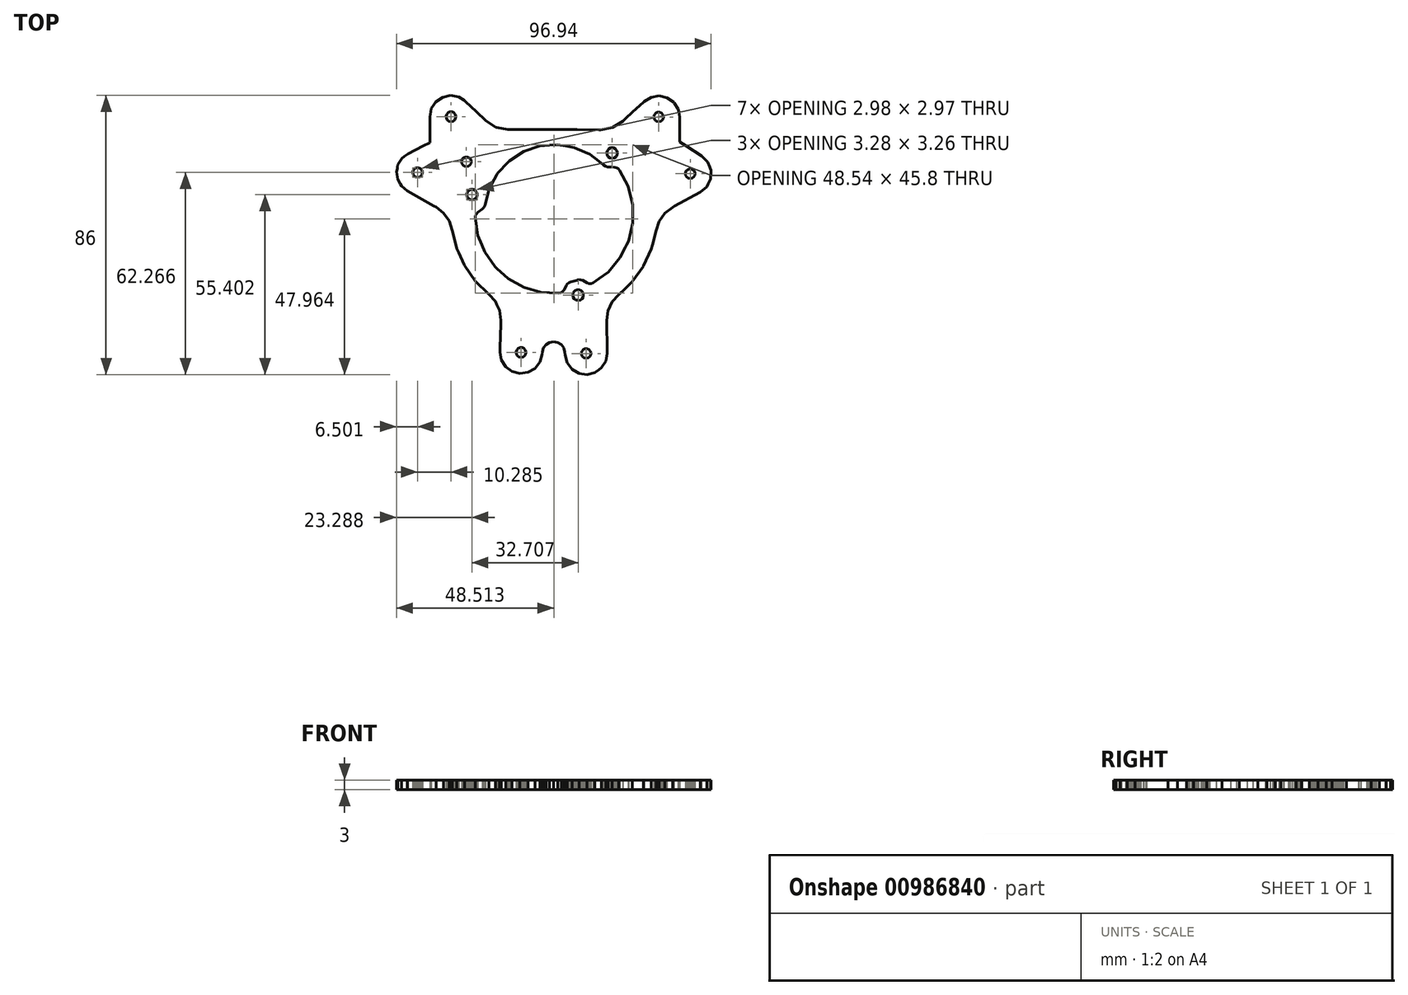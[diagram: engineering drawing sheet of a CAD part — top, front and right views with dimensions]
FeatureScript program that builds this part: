
annotation { "Feature Type Name" : "Feature", "Feature Type Description" : "" }
export const myFeature = defineFeature(function(context is Context, id is Id, definition is map)
    precondition{}
    {
        {
            var Q0;
            Q0=qCreatedBy(makeId("Top.planeOp"),FACE);
            var sketch = newSketch(context, id + "F0", { "sketchPlane" : qUnion([Q0])});
            skLineSegment(sketch, "E0", {"start": v(-20, -18.27) * mm, "end": v(-17.98, -20.51) * mm});
            skLineSegment(sketch, "E1", {"start": v(-17.98, -20.51) * mm, "end": v(-17.54, -21.47) * mm});
            skLineSegment(sketch, "E2", {"start": v(-17.54, -21.47) * mm, "end": v(-16.72, -23.25) * mm});
            skLineSegment(sketch, "E3", {"start": v(-16.72, -23.25) * mm, "end": v(-16.33, -26.24) * mm});
            skLineSegment(sketch, "E4", {"start": v(-20.99, 35.26) * mm, "end": v(-23.77, 37.92) * mm});
            skLineSegment(sketch, "E5", {"start": v(-23.77, 37.92) * mm, "end": v(-27.19, 41.2) * mm});
            skLineSegment(sketch, "E6", {"start": v(-24.23, 5.27) * mm, "end": v(-24.15, 5.93) * mm});
            skLineSegment(sketch, "E7", {"start": v(-24.15, 5.93) * mm, "end": v(-23.85, 6.53) * mm});
            skLineSegment(sketch, "E8", {"start": v(-23.85, 6.53) * mm, "end": v(-23.38, 7) * mm});
            skLineSegment(sketch, "E9", {"start": v(38.82, 28.73) * mm, "end": v(38.82, 31.38) * mm});
            skLineSegment(sketch, "E10", {"start": v(38.82, 31.38) * mm, "end": v(38.82, 36.37) * mm});
            skLineSegment(sketch, "E11", {"start": v(3.87, -15.55) * mm, "end": v(3.21, -16.84) * mm});
            skLineSegment(sketch, "E12", {"start": v(10.22, -14.77) * mm, "end": v(8.92, -14.03) * mm});
            skLineSegment(sketch, "E13", {"start": v(27.92, 41.18) * mm, "end": v(27.64, 40.92) * mm});
            skLineSegment(sketch, "E14", {"start": v(27.64, 40.92) * mm, "end": v(24.37, 37.92) * mm});
            skLineSegment(sketch, "E15", {"start": v(24.37, 37.92) * mm, "end": v(22.05, 35.79) * mm});
            skLineSegment(sketch, "E16", {"start": v(22.05, 35.79) * mm, "end": v(21.26, 35.07) * mm});
            skLineSegment(sketch, "E17", {"start": v(-38.18, 36.5) * mm, "end": v(-38.18, 31.38) * mm});
            skLineSegment(sketch, "E18", {"start": v(-38.18, 31.38) * mm, "end": v(-38.18, 28.5) * mm});
            skLineSegment(sketch, "E19", {"start": v(20.06, -18.4) * mm, "end": v(22.05, -16.48) * mm});
            skLineSegment(sketch, "E20", {"start": v(22.05, -16.48) * mm, "end": v(24.25, -14.35) * mm});
            skLineSegment(sketch, "E21", {"start": v(24.25, -14.35) * mm, "end": v(27.63, -9.6) * mm});
            skLineSegment(sketch, "E22", {"start": v(27.63, -9.6) * mm, "end": v(27.64, -9.56) * mm});
            skLineSegment(sketch, "E23", {"start": v(27.64, -9.56) * mm, "end": v(30.08, -4.3) * mm});
            skLineSegment(sketch, "E24", {"start": v(30.08, -4.3) * mm, "end": v(30.4, -3.06) * mm});
            skLineSegment(sketch, "E25", {"start": v(30.4, -3.06) * mm, "end": v(31.53, 1.35) * mm});
            skLineSegment(sketch, "E26", {"start": v(-44.91, 25.08) * mm, "end": v(-45.97, 24.27) * mm});
            skLineSegment(sketch, "E27", {"start": v(-45.97, 24.27) * mm, "end": v(-46.76, 23.67) * mm});
            skLineSegment(sketch, "E28", {"start": v(-46.76, 23.67) * mm, "end": v(-48, 21.7) * mm});
            skLineSegment(sketch, "E29", {"start": v(-48, 21.7) * mm, "end": v(-48.16, 20.92) * mm});
            skLineSegment(sketch, "E30", {"start": v(-48.16, 20.92) * mm, "end": v(-48.23, 20.58) * mm});
            skLineSegment(sketch, "E31", {"start": v(-48.23, 20.58) * mm, "end": v(-48.47, 19.43) * mm});
            skLineSegment(sketch, "E32", {"start": v(-48.47, 19.43) * mm, "end": v(-48.1, 17.14) * mm});
            skLineSegment(sketch, "E33", {"start": v(-48.1, 17.14) * mm, "end": v(-47.3, 15.72) * mm});
            skLineSegment(sketch, "E34", {"start": v(-47.3, 15.72) * mm, "end": v(-46.96, 15.11) * mm});
            skLineSegment(sketch, "E35", {"start": v(-46.96, 15.11) * mm, "end": v(-45.97, 14.3) * mm});
            skLineSegment(sketch, "E36", {"start": v(-45.97, 14.3) * mm, "end": v(-45.17, 13.63) * mm});
            skLineSegment(sketch, "E37", {"start": v(-24.51, 10.91) * mm, "end": v(-25.18, 10.77) * mm});
            skLineSegment(sketch, "E38", {"start": v(-25.18, 10.77) * mm, "end": v(-25.85, 10.91) * mm});
            skLineSegment(sketch, "E39", {"start": v(-25.85, 10.91) * mm, "end": v(-26.4, 11.32) * mm});
            skLineSegment(sketch, "E40", {"start": v(-26.4, 11.32) * mm, "end": v(-26.75, 11.91) * mm});
            skLineSegment(sketch, "E41", {"start": v(-26.75, 11.91) * mm, "end": v(-26.82, 12.6) * mm});
            skLineSegment(sketch, "E42", {"start": v(-26.82, 12.6) * mm, "end": v(-26.61, 13.25) * mm});
            skLineSegment(sketch, "E43", {"start": v(-26.61, 13.25) * mm, "end": v(-26.15, 13.76) * mm});
            skLineSegment(sketch, "E44", {"start": v(-26.15, 13.76) * mm, "end": v(-25.53, 14.03) * mm});
            skLineSegment(sketch, "E45", {"start": v(-25.53, 14.03) * mm, "end": v(-24.84, 14.03) * mm});
            skLineSegment(sketch, "E46", {"start": v(-24.84, 14.03) * mm, "end": v(-24.21, 13.76) * mm});
            skLineSegment(sketch, "E47", {"start": v(-24.21, 13.76) * mm, "end": v(-23.75, 13.25) * mm});
            skLineSegment(sketch, "E48", {"start": v(-23.75, 13.25) * mm, "end": v(-23.54, 12.6) * mm});
            skLineSegment(sketch, "E49", {"start": v(-23.54, 12.6) * mm, "end": v(-23.61, 11.91) * mm});
            skLineSegment(sketch, "E50", {"start": v(-23.61, 11.91) * mm, "end": v(-23.96, 11.32) * mm});
            skLineSegment(sketch, "E51", {"start": v(-23.96, 11.32) * mm, "end": v(-24.51, 10.91) * mm});
            skLineSegment(sketch, "E52", {"start": v(20.33, 19.96) * mm, "end": v(22.05, 16.62) * mm});
            skLineSegment(sketch, "E53", {"start": v(22.05, 16.62) * mm, "end": v(22.5, 15.72) * mm});
            skLineSegment(sketch, "E54", {"start": v(22.5, 15.72) * mm, "end": v(22.93, 14.89) * mm});
            skLineSegment(sketch, "E55", {"start": v(22.93, 14.89) * mm, "end": v(24.29, 9.35) * mm});
            skLineSegment(sketch, "E56", {"start": v(24.29, 9.35) * mm, "end": v(24.31, 3.64) * mm});
            skLineSegment(sketch, "E57", {"start": v(24.31, 3.64) * mm, "end": v(23.01, -1.91) * mm});
            skLineSegment(sketch, "E58", {"start": v(23.01, -1.91) * mm, "end": v(22.44, -3.06) * mm});
            skLineSegment(sketch, "E59", {"start": v(22.44, -3.06) * mm, "end": v(22.05, -3.83) * mm});
            skLineSegment(sketch, "E60", {"start": v(22.05, -3.83) * mm, "end": v(20.46, -7) * mm});
            skLineSegment(sketch, "E61", {"start": v(20.46, -7) * mm, "end": v(16.78, -11.37) * mm});
            skLineSegment(sketch, "E62", {"start": v(16.78, -11.37) * mm, "end": v(13.9, -13.5) * mm});
            skLineSegment(sketch, "E63", {"start": v(13.9, -13.5) * mm, "end": v(12.2, -14.77) * mm});
            skLineSegment(sketch, "E64", {"start": v(16.58, 21) * mm, "end": v(17.73, 20.92) * mm});
            skLineSegment(sketch, "E65", {"start": v(17.73, 20.92) * mm, "end": v(18.81, 20.84) * mm});
            skLineSegment(sketch, "E66", {"start": v(-22.03, 7.95) * mm, "end": v(-21.47, 8.54) * mm});
            skLineSegment(sketch, "E67", {"start": v(-21.47, 8.54) * mm, "end": v(-21.2, 9.31) * mm});
            skLineSegment(sketch, "E68", {"start": v(8.92, -14.03) * mm, "end": v(8.4, -13.83) * mm});
            skLineSegment(sketch, "E69", {"start": v(8.4, -13.83) * mm, "end": v(7.83, -13.78) * mm});
            skLineSegment(sketch, "E70", {"start": v(7.83, -13.78) * mm, "end": v(7.27, -13.89) * mm});
            skLineSegment(sketch, "E71", {"start": v(12.2, -14.77) * mm, "end": v(11.55, -15) * mm});
            skLineSegment(sketch, "E72", {"start": v(11.55, -15) * mm, "end": v(10.86, -15) * mm});
            skLineSegment(sketch, "E73", {"start": v(10.86, -15) * mm, "end": v(10.22, -14.77) * mm});
            skLineSegment(sketch, "E74", {"start": v(3.5, -37.01) * mm, "end": v(4.16, -39.4) * mm});
            skLineSegment(sketch, "E75", {"start": v(4.16, -39.4) * mm, "end": v(5.67, -41.38) * mm});
            skLineSegment(sketch, "E76", {"start": v(5.67, -41.38) * mm, "end": v(7.18, -42.26) * mm});
            skLineSegment(sketch, "E77", {"start": v(7.18, -42.26) * mm, "end": v(7.82, -42.64) * mm});
            skLineSegment(sketch, "E78", {"start": v(7.82, -42.64) * mm, "end": v(10.28, -43) * mm});
            skLineSegment(sketch, "E79", {"start": v(10.28, -43) * mm, "end": v(12.7, -42.41) * mm});
            skLineSegment(sketch, "E80", {"start": v(12.7, -42.41) * mm, "end": v(13.9, -41.54) * mm});
            skLineSegment(sketch, "E81", {"start": v(13.9, -41.54) * mm, "end": v(14.7, -40.96) * mm});
            skLineSegment(sketch, "E82", {"start": v(14.7, -40.96) * mm, "end": v(16.04, -38.86) * mm});
            skLineSegment(sketch, "E83", {"start": v(16.04, -38.86) * mm, "end": v(16.48, -36.41) * mm});
            skLineSegment(sketch, "E84", {"start": v(-31.33, 1.44) * mm, "end": v(-30.2, -3.06) * mm});
            skLineSegment(sketch, "E85", {"start": v(-30.2, -3.06) * mm, "end": v(-29.9, -4.19) * mm});
            skLineSegment(sketch, "E86", {"start": v(-29.9, -4.19) * mm, "end": v(-29.3, -5.5) * mm});
            skLineSegment(sketch, "E87", {"start": v(-29.3, -5.5) * mm, "end": v(-27.63, -9.16) * mm});
            skLineSegment(sketch, "E88", {"start": v(-27.63, -9.16) * mm, "end": v(-27.49, -9.46) * mm});
            skLineSegment(sketch, "E89", {"start": v(-27.49, -9.46) * mm, "end": v(-24.15, -14.2) * mm});
            skLineSegment(sketch, "E90", {"start": v(-24.15, -14.2) * mm, "end": v(-20, -18.27) * mm});
            skLineSegment(sketch, "E91", {"start": v(7.52, -20.19) * mm, "end": v(7.18, -20.11) * mm});
            skLineSegment(sketch, "E92", {"start": v(7.18, -20.11) * mm, "end": v(6.85, -20.04) * mm});
            skLineSegment(sketch, "E93", {"start": v(6.85, -20.04) * mm, "end": v(6.3, -19.64) * mm});
            skLineSegment(sketch, "E94", {"start": v(6.3, -19.64) * mm, "end": v(5.96, -19.05) * mm});
            skLineSegment(sketch, "E95", {"start": v(5.96, -19.05) * mm, "end": v(5.88, -18.36) * mm});
            skLineSegment(sketch, "E96", {"start": v(5.88, -18.36) * mm, "end": v(6.1, -17.71) * mm});
            skLineSegment(sketch, "E97", {"start": v(6.1, -17.71) * mm, "end": v(6.56, -17.2) * mm});
            skLineSegment(sketch, "E98", {"start": v(6.56, -17.2) * mm, "end": v(7.18, -16.92) * mm});
            skLineSegment(sketch, "E99", {"start": v(7.18, -16.92) * mm, "end": v(7.18, -16.92) * mm});
            skLineSegment(sketch, "E100", {"start": v(7.18, -16.92) * mm, "end": v(7.87, -16.92) * mm});
            skLineSegment(sketch, "E101", {"start": v(7.87, -16.92) * mm, "end": v(8.5, -17.2) * mm});
            skLineSegment(sketch, "E102", {"start": v(8.5, -17.2) * mm, "end": v(8.95, -17.71) * mm});
            skLineSegment(sketch, "E103", {"start": v(8.95, -17.71) * mm, "end": v(9.17, -18.36) * mm});
            skLineSegment(sketch, "E104", {"start": v(9.17, -18.36) * mm, "end": v(9.1, -19.05) * mm});
            skLineSegment(sketch, "E105", {"start": v(9.1, -19.05) * mm, "end": v(8.75, -19.64) * mm});
            skLineSegment(sketch, "E106", {"start": v(8.75, -19.64) * mm, "end": v(8.2, -20.04) * mm});
            skLineSegment(sketch, "E107", {"start": v(8.2, -20.04) * mm, "end": v(7.52, -20.19) * mm});
            skLineSegment(sketch, "E108", {"start": v(31.7, 35) * mm, "end": v(31.2, 35.37) * mm});
            skLineSegment(sketch, "E109", {"start": v(31.2, 35.37) * mm, "end": v(30.89, 35.91) * mm});
            skLineSegment(sketch, "E110", {"start": v(30.89, 35.91) * mm, "end": v(30.82, 36.53) * mm});
            skLineSegment(sketch, "E111", {"start": v(30.82, 36.53) * mm, "end": v(31.02, 37.12) * mm});
            skLineSegment(sketch, "E112", {"start": v(31.02, 37.12) * mm, "end": v(31.43, 37.59) * mm});
            skLineSegment(sketch, "E113", {"start": v(31.43, 37.59) * mm, "end": v(32, 37.84) * mm});
            skLineSegment(sketch, "E114", {"start": v(32, 37.84) * mm, "end": v(32.63, 37.84) * mm});
            skLineSegment(sketch, "E115", {"start": v(32.63, 37.84) * mm, "end": v(33.2, 37.59) * mm});
            skLineSegment(sketch, "E116", {"start": v(33.2, 37.59) * mm, "end": v(33.62, 37.12) * mm});
            skLineSegment(sketch, "E117", {"start": v(33.62, 37.12) * mm, "end": v(33.8, 36.53) * mm});
            skLineSegment(sketch, "E118", {"start": v(33.8, 36.53) * mm, "end": v(33.74, 35.91) * mm});
            skLineSegment(sketch, "E119", {"start": v(33.74, 35.91) * mm, "end": v(33.43, 35.37) * mm});
            skLineSegment(sketch, "E120", {"start": v(33.43, 35.37) * mm, "end": v(32.93, 35) * mm});
            skLineSegment(sketch, "E121", {"start": v(32.93, 35) * mm, "end": v(32.32, 34.87) * mm});
            skLineSegment(sketch, "E122", {"start": v(32.32, 34.87) * mm, "end": v(31.7, 35) * mm});
            skLineSegment(sketch, "E123", {"start": v(9.37, -37.88) * mm, "end": v(8.86, -37.5) * mm});
            skLineSegment(sketch, "E124", {"start": v(8.86, -37.5) * mm, "end": v(8.55, -36.97) * mm});
            skLineSegment(sketch, "E125", {"start": v(8.55, -36.97) * mm, "end": v(8.48, -36.35) * mm});
            skLineSegment(sketch, "E126", {"start": v(8.48, -36.35) * mm, "end": v(8.68, -35.75) * mm});
            skLineSegment(sketch, "E127", {"start": v(8.68, -35.75) * mm, "end": v(9.1, -35.3) * mm});
            skLineSegment(sketch, "E128", {"start": v(9.1, -35.3) * mm, "end": v(9.66, -35.04) * mm});
            skLineSegment(sketch, "E129", {"start": v(9.66, -35.04) * mm, "end": v(10.29, -35.04) * mm});
            skLineSegment(sketch, "E130", {"start": v(10.29, -35.04) * mm, "end": v(10.86, -35.3) * mm});
            skLineSegment(sketch, "E131", {"start": v(10.86, -35.3) * mm, "end": v(11.28, -35.75) * mm});
            skLineSegment(sketch, "E132", {"start": v(11.28, -35.75) * mm, "end": v(11.47, -36.35) * mm});
            skLineSegment(sketch, "E133", {"start": v(11.47, -36.35) * mm, "end": v(11.4, -36.97) * mm});
            skLineSegment(sketch, "E134", {"start": v(11.4, -36.97) * mm, "end": v(11.1, -37.5) * mm});
            skLineSegment(sketch, "E135", {"start": v(11.1, -37.5) * mm, "end": v(10.59, -37.88) * mm});
            skLineSegment(sketch, "E136", {"start": v(10.59, -37.88) * mm, "end": v(9.98, -38) * mm});
            skLineSegment(sketch, "E137", {"start": v(9.98, -38) * mm, "end": v(9.37, -37.88) * mm});
            skLineSegment(sketch, "E138", {"start": v(18.81, 20.84) * mm, "end": v(19.4, 20.71) * mm});
            skLineSegment(sketch, "E139", {"start": v(19.4, 20.71) * mm, "end": v(19.63, 20.58) * mm});
            skLineSegment(sketch, "E140", {"start": v(19.63, 20.58) * mm, "end": v(19.92, 20.4) * mm});
            skLineSegment(sketch, "E141", {"start": v(19.92, 20.4) * mm, "end": v(20.33, 19.96) * mm});
            skLineSegment(sketch, "E142", {"start": v(-16.33, -26.24) * mm, "end": v(-16.36, -27.44) * mm});
            skLineSegment(sketch, "E143", {"start": v(-16.36, -27.44) * mm, "end": v(-16.52, -34.85) * mm});
            skLineSegment(sketch, "E144", {"start": v(-16.52, -34.85) * mm, "end": v(-16.55, -36.05) * mm});
            skLineSegment(sketch, "E145", {"start": v(17.3, 23.76) * mm, "end": v(16.75, 24.16) * mm});
            skLineSegment(sketch, "E146", {"start": v(16.75, 24.16) * mm, "end": v(16.41, 24.76) * mm});
            skLineSegment(sketch, "E147", {"start": v(16.41, 24.76) * mm, "end": v(16.34, 25.44) * mm});
            skLineSegment(sketch, "E148", {"start": v(16.34, 25.44) * mm, "end": v(16.55, 26.1) * mm});
            skLineSegment(sketch, "E149", {"start": v(16.55, 26.1) * mm, "end": v(17.01, 26.6) * mm});
            skLineSegment(sketch, "E150", {"start": v(17.01, 26.6) * mm, "end": v(17.64, 26.88) * mm});
            skLineSegment(sketch, "E151", {"start": v(17.64, 26.88) * mm, "end": v(18.32, 26.88) * mm});
            skLineSegment(sketch, "E152", {"start": v(18.32, 26.88) * mm, "end": v(18.95, 26.6) * mm});
            skLineSegment(sketch, "E153", {"start": v(18.95, 26.6) * mm, "end": v(19.4, 26.1) * mm});
            skLineSegment(sketch, "E154", {"start": v(19.4, 26.1) * mm, "end": v(19.62, 25.44) * mm});
            skLineSegment(sketch, "E155", {"start": v(19.62, 25.44) * mm, "end": v(19.55, 24.76) * mm});
            skLineSegment(sketch, "E156", {"start": v(19.55, 24.76) * mm, "end": v(19.2, 24.16) * mm});
            skLineSegment(sketch, "E157", {"start": v(19.2, 24.16) * mm, "end": v(18.65, 23.76) * mm});
            skLineSegment(sketch, "E158", {"start": v(18.65, 23.76) * mm, "end": v(17.98, 23.62) * mm});
            skLineSegment(sketch, "E159", {"start": v(17.98, 23.62) * mm, "end": v(17.3, 23.76) * mm});
            skLineSegment(sketch, "E160", {"start": v(-21.2, 9.31) * mm, "end": v(-19.83, 14.42) * mm});
            skLineSegment(sketch, "E161", {"start": v(-19.83, 14.42) * mm, "end": v(-19.11, 15.72) * mm});
            skLineSegment(sketch, "E162", {"start": v(-19.11, 15.72) * mm, "end": v(-17.54, 18.55) * mm});
            skLineSegment(sketch, "E163", {"start": v(-17.54, 18.55) * mm, "end": v(-17.27, 19.05) * mm});
            skLineSegment(sketch, "E164", {"start": v(-17.27, 19.05) * mm, "end": v(-15.83, 20.58) * mm});
            skLineSegment(sketch, "E165", {"start": v(-15.83, 20.58) * mm, "end": v(-15.5, 20.92) * mm});
            skLineSegment(sketch, "E166", {"start": v(-15.5, 20.92) * mm, "end": v(-13.65, 22.9) * mm});
            skLineSegment(sketch, "E167", {"start": v(-13.65, 22.9) * mm, "end": v(-9.2, 25.77) * mm});
            skLineSegment(sketch, "E168", {"start": v(-9.2, 25.77) * mm, "end": v(-4.34, 27.4) * mm});
            skLineSegment(sketch, "E169", {"start": v(-4.34, 27.4) * mm, "end": v(-4.19, 27.45) * mm});
            skLineSegment(sketch, "E170", {"start": v(-4.19, 27.45) * mm, "end": v(-1.34, 27.67) * mm});
            skLineSegment(sketch, "E171", {"start": v(-1.34, 27.67) * mm, "end": v(1.09, 27.86) * mm});
            skLineSegment(sketch, "E172", {"start": v(1.09, 27.86) * mm, "end": v(3.8, 27.4) * mm});
            skLineSegment(sketch, "E173", {"start": v(3.8, 27.4) * mm, "end": v(6.3, 26.97) * mm});
            skLineSegment(sketch, "E174", {"start": v(6.3, 26.97) * mm, "end": v(7.18, 26.59) * mm});
            skLineSegment(sketch, "E175", {"start": v(7.18, 26.59) * mm, "end": v(11.14, 24.84) * mm});
            skLineSegment(sketch, "E176", {"start": v(11.14, 24.84) * mm, "end": v(13.9, 22.68) * mm});
            skLineSegment(sketch, "E177", {"start": v(13.9, 22.68) * mm, "end": v(15.31, 21.58) * mm});
            skLineSegment(sketch, "E178", {"start": v(45.6, 24.32) * mm, "end": v(40.87, 27.4) * mm});
            skLineSegment(sketch, "E179", {"start": v(40.87, 27.4) * mm, "end": v(38.82, 28.73) * mm});
            skLineSegment(sketch, "E180", {"start": v(-16.55, -36.05) * mm, "end": v(-16.13, -38.5) * mm});
            skLineSegment(sketch, "E181", {"start": v(-16.13, -38.5) * mm, "end": v(-14.82, -40.6) * mm});
            skLineSegment(sketch, "E182", {"start": v(-14.82, -40.6) * mm, "end": v(-12.82, -42.07) * mm});
            skLineSegment(sketch, "E183", {"start": v(-12.82, -42.07) * mm, "end": v(-10.42, -42.68) * mm});
            skLineSegment(sketch, "E184", {"start": v(-10.42, -42.68) * mm, "end": v(-7.96, -42.35) * mm});
            skLineSegment(sketch, "E185", {"start": v(-7.96, -42.35) * mm, "end": v(-5.8, -41.11) * mm});
            skLineSegment(sketch, "E186", {"start": v(-5.8, -41.11) * mm, "end": v(-4.27, -39.17) * mm});
            skLineSegment(sketch, "E187", {"start": v(-4.27, -39.17) * mm, "end": v(-3.58, -36.78) * mm});
            skLineSegment(sketch, "E188", {"start": v(15.31, 21.58) * mm, "end": v(15.9, 21.18) * mm});
            skLineSegment(sketch, "E189", {"start": v(15.9, 21.18) * mm, "end": v(16.58, 21) * mm});
            skLineSegment(sketch, "E190", {"start": v(5.18, -14.5) * mm, "end": v(4.65, -14.72) * mm});
            skLineSegment(sketch, "E191", {"start": v(4.65, -14.72) * mm, "end": v(4.2, -15.08) * mm});
            skLineSegment(sketch, "E192", {"start": v(4.2, -15.08) * mm, "end": v(3.87, -15.55) * mm});
            skLineSegment(sketch, "E193", {"start": v(16.48, -36.41) * mm, "end": v(16.45, -34.85) * mm});
            skLineSegment(sketch, "E194", {"start": v(16.45, -34.85) * mm, "end": v(16.35, -27.44) * mm});
            skLineSegment(sketch, "E195", {"start": v(16.35, -27.44) * mm, "end": v(16.33, -26.34) * mm});
            skLineSegment(sketch, "E196", {"start": v(7.27, -13.89) * mm, "end": v(7.18, -13.92) * mm});
            skLineSegment(sketch, "E197", {"start": v(7.18, -13.92) * mm, "end": v(5.18, -14.5) * mm});
            skLineSegment(sketch, "E198", {"start": v(-3.51, -36.07) * mm, "end": v(-3.16, -34.85) * mm});
            skLineSegment(sketch, "E199", {"start": v(-3.16, -34.85) * mm, "end": v(-3.16, -34.83) * mm});
            skLineSegment(sketch, "E200", {"start": v(-3.16, -34.83) * mm, "end": v(-2.38, -33.8) * mm});
            skLineSegment(sketch, "E201", {"start": v(-2.38, -33.8) * mm, "end": v(-1.34, -33.17) * mm});
            skLineSegment(sketch, "E202", {"start": v(-1.34, -33.17) * mm, "end": v(-1.29, -33.14) * mm});
            skLineSegment(sketch, "E203", {"start": v(-1.29, -33.14) * mm, "end": v(-0.02, -32.9) * mm});
            skLineSegment(sketch, "E204", {"start": v(-0.02, -32.9) * mm, "end": v(1.24, -33.15) * mm});
            skLineSegment(sketch, "E205", {"start": v(1.24, -33.15) * mm, "end": v(2.33, -33.84) * mm});
            skLineSegment(sketch, "E206", {"start": v(2.33, -33.84) * mm, "end": v(3.07, -34.85) * mm});
            skLineSegment(sketch, "E207", {"start": v(3.07, -34.85) * mm, "end": v(3.1, -34.88) * mm});
            skLineSegment(sketch, "E208", {"start": v(3.1, -34.88) * mm, "end": v(3.43, -36.12) * mm});
            skLineSegment(sketch, "E209", {"start": v(-36.28, 8.59) * mm, "end": v(-33.93, 6.74) * mm});
            skLineSegment(sketch, "E210", {"start": v(-33.93, 6.74) * mm, "end": v(-32.23, 4.29) * mm});
            skLineSegment(sketch, "E211", {"start": v(-32.23, 4.29) * mm, "end": v(-31.33, 1.44) * mm});
            skLineSegment(sketch, "E212", {"start": v(-45.17, 13.63) * mm, "end": v(-36.83, 8.9) * mm});
            skLineSegment(sketch, "E213", {"start": v(-36.83, 8.9) * mm, "end": v(-36.28, 8.59) * mm});
            skLineSegment(sketch, "E214", {"start": v(3.21, -16.84) * mm, "end": v(2.8, -17.4) * mm});
            skLineSegment(sketch, "E215", {"start": v(2.8, -17.4) * mm, "end": v(2.22, -17.77) * mm});
            skLineSegment(sketch, "E216", {"start": v(2.22, -17.77) * mm, "end": v(1.55, -17.93) * mm});
            skLineSegment(sketch, "E217", {"start": v(45.15, 13.15) * mm, "end": v(47.19, 14.88) * mm});
            skLineSegment(sketch, "E218", {"start": v(47.19, 14.88) * mm, "end": v(47.6, 15.72) * mm});
            skLineSegment(sketch, "E219", {"start": v(47.6, 15.72) * mm, "end": v(48.36, 17.28) * mm});
            skLineSegment(sketch, "E220", {"start": v(48.36, 17.28) * mm, "end": v(48.47, 19.95) * mm});
            skLineSegment(sketch, "E221", {"start": v(48.47, 19.95) * mm, "end": v(48.22, 20.58) * mm});
            skLineSegment(sketch, "E222", {"start": v(48.22, 20.58) * mm, "end": v(48.09, 20.92) * mm});
            skLineSegment(sketch, "E223", {"start": v(48.09, 20.92) * mm, "end": v(47.5, 22.44) * mm});
            skLineSegment(sketch, "E224", {"start": v(47.5, 22.44) * mm, "end": v(45.6, 24.32) * mm});
            skLineSegment(sketch, "E225", {"start": v(-10.36, -34.72) * mm, "end": v(-9.74, -34.72) * mm});
            skLineSegment(sketch, "E226", {"start": v(-9.74, -34.72) * mm, "end": v(-9.46, -34.85) * mm});
            skLineSegment(sketch, "E227", {"start": v(-9.46, -34.85) * mm, "end": v(-9.17, -34.98) * mm});
            skLineSegment(sketch, "E228", {"start": v(-9.17, -34.98) * mm, "end": v(-8.75, -35.44) * mm});
            skLineSegment(sketch, "E229", {"start": v(-8.75, -35.44) * mm, "end": v(-8.56, -36.03) * mm});
            skLineSegment(sketch, "E230", {"start": v(-8.56, -36.03) * mm, "end": v(-8.62, -36.65) * mm});
            skLineSegment(sketch, "E231", {"start": v(-8.62, -36.65) * mm, "end": v(-8.94, -37.2) * mm});
            skLineSegment(sketch, "E232", {"start": v(-8.94, -37.2) * mm, "end": v(-9.44, -37.56) * mm});
            skLineSegment(sketch, "E233", {"start": v(-9.44, -37.56) * mm, "end": v(-10.05, -37.7) * mm});
            skLineSegment(sketch, "E234", {"start": v(-10.05, -37.7) * mm, "end": v(-10.66, -37.56) * mm});
            skLineSegment(sketch, "E235", {"start": v(-10.66, -37.56) * mm, "end": v(-11.16, -37.2) * mm});
            skLineSegment(sketch, "E236", {"start": v(-11.16, -37.2) * mm, "end": v(-11.48, -36.65) * mm});
            skLineSegment(sketch, "E237", {"start": v(-11.48, -36.65) * mm, "end": v(-11.54, -36.03) * mm});
            skLineSegment(sketch, "E238", {"start": v(-11.54, -36.03) * mm, "end": v(-11.35, -35.44) * mm});
            skLineSegment(sketch, "E239", {"start": v(-11.35, -35.44) * mm, "end": v(-10.93, -34.98) * mm});
            skLineSegment(sketch, "E240", {"start": v(-10.93, -34.98) * mm, "end": v(-10.64, -34.85) * mm});
            skLineSegment(sketch, "E241", {"start": v(-10.64, -34.85) * mm, "end": v(-10.36, -34.72) * mm});
            skLineSegment(sketch, "E242", {"start": v(-23.38, 7) * mm, "end": v(-22.03, 7.95) * mm});
            skLineSegment(sketch, "E243", {"start": v(-14.09, 32.48) * mm, "end": v(-17.54, 33.15) * mm});
            skLineSegment(sketch, "E244", {"start": v(-17.54, 33.15) * mm, "end": v(-17.8, 33.2) * mm});
            skLineSegment(sketch, "E245", {"start": v(-17.8, 33.2) * mm, "end": v(-20.99, 35.26) * mm});
            skLineSegment(sketch, "E246", {"start": v(36.65, 8.57) * mm, "end": v(37.19, 8.86) * mm});
            skLineSegment(sketch, "E247", {"start": v(37.19, 8.86) * mm, "end": v(45.15, 13.15) * mm});
            skLineSegment(sketch, "E248", {"start": v(41.45, 17.5) * mm, "end": v(40.94, 17.87) * mm});
            skLineSegment(sketch, "E249", {"start": v(40.94, 17.87) * mm, "end": v(40.63, 18.41) * mm});
            skLineSegment(sketch, "E250", {"start": v(40.63, 18.41) * mm, "end": v(40.57, 19.03) * mm});
            skLineSegment(sketch, "E251", {"start": v(40.57, 19.03) * mm, "end": v(40.76, 19.62) * mm});
            skLineSegment(sketch, "E252", {"start": v(40.76, 19.62) * mm, "end": v(41.18, 20.09) * mm});
            skLineSegment(sketch, "E253", {"start": v(41.18, 20.09) * mm, "end": v(41.75, 20.34) * mm});
            skLineSegment(sketch, "E254", {"start": v(41.75, 20.34) * mm, "end": v(42.37, 20.34) * mm});
            skLineSegment(sketch, "E255", {"start": v(42.37, 20.34) * mm, "end": v(42.94, 20.09) * mm});
            skLineSegment(sketch, "E256", {"start": v(42.94, 20.09) * mm, "end": v(43.36, 19.62) * mm});
            skLineSegment(sketch, "E257", {"start": v(43.36, 19.62) * mm, "end": v(43.55, 19.03) * mm});
            skLineSegment(sketch, "E258", {"start": v(43.55, 19.03) * mm, "end": v(43.48, 18.41) * mm});
            skLineSegment(sketch, "E259", {"start": v(43.48, 18.41) * mm, "end": v(43.17, 17.87) * mm});
            skLineSegment(sketch, "E260", {"start": v(43.17, 17.87) * mm, "end": v(42.67, 17.5) * mm});
            skLineSegment(sketch, "E261", {"start": v(42.67, 17.5) * mm, "end": v(42.06, 17.37) * mm});
            skLineSegment(sketch, "E262", {"start": v(42.06, 17.37) * mm, "end": v(41.45, 17.5) * mm});
            skLineSegment(sketch, "E263", {"start": v(-26.92, 21.06) * mm, "end": v(-27.53, 21.2) * mm});
            skLineSegment(sketch, "E264", {"start": v(-27.53, 21.2) * mm, "end": v(-27.63, 21.26) * mm});
            skLineSegment(sketch, "E265", {"start": v(-27.63, 21.26) * mm, "end": v(-28.03, 21.56) * mm});
            skLineSegment(sketch, "E266", {"start": v(-28.03, 21.56) * mm, "end": v(-28.35, 22.1) * mm});
            skLineSegment(sketch, "E267", {"start": v(-28.35, 22.1) * mm, "end": v(-28.41, 22.72) * mm});
            skLineSegment(sketch, "E268", {"start": v(-28.41, 22.72) * mm, "end": v(-28.22, 23.31) * mm});
            skLineSegment(sketch, "E269", {"start": v(-28.22, 23.31) * mm, "end": v(-27.8, 23.78) * mm});
            skLineSegment(sketch, "E270", {"start": v(-27.8, 23.78) * mm, "end": v(-27.63, 23.85) * mm});
            skLineSegment(sketch, "E271", {"start": v(-27.63, 23.85) * mm, "end": v(-27.23, 24.03) * mm});
            skLineSegment(sketch, "E272", {"start": v(-27.23, 24.03) * mm, "end": v(-26.6, 24.03) * mm});
            skLineSegment(sketch, "E273", {"start": v(-26.6, 24.03) * mm, "end": v(-26.04, 23.78) * mm});
            skLineSegment(sketch, "E274", {"start": v(-26.04, 23.78) * mm, "end": v(-25.62, 23.31) * mm});
            skLineSegment(sketch, "E275", {"start": v(-25.62, 23.31) * mm, "end": v(-25.43, 22.72) * mm});
            skLineSegment(sketch, "E276", {"start": v(-25.43, 22.72) * mm, "end": v(-25.5, 22.1) * mm});
            skLineSegment(sketch, "E277", {"start": v(-25.5, 22.1) * mm, "end": v(-25.8, 21.56) * mm});
            skLineSegment(sketch, "E278", {"start": v(-25.8, 21.56) * mm, "end": v(-26.3, 21.2) * mm});
            skLineSegment(sketch, "E279", {"start": v(-26.3, 21.2) * mm, "end": v(-26.92, 21.06) * mm});
            skLineSegment(sketch, "E280", {"start": v(31.53, 1.35) * mm, "end": v(32.46, 4.25) * mm});
            skLineSegment(sketch, "E281", {"start": v(32.46, 4.25) * mm, "end": v(34.22, 6.73) * mm});
            skLineSegment(sketch, "E282", {"start": v(34.22, 6.73) * mm, "end": v(36.65, 8.57) * mm});
            skLineSegment(sketch, "E283", {"start": v(1.55, -17.93) * mm, "end": v(-1.34, -17.78) * mm});
            skLineSegment(sketch, "E284", {"start": v(-1.34, -17.78) * mm, "end": v(-3.95, -17.64) * mm});
            skLineSegment(sketch, "E285", {"start": v(-3.95, -17.64) * mm, "end": v(-9.23, -16.11) * mm});
            skLineSegment(sketch, "E286", {"start": v(-9.23, -16.11) * mm, "end": v(-14.04, -13.45) * mm});
            skLineSegment(sketch, "E287", {"start": v(-14.04, -13.45) * mm, "end": v(-17.54, -10.3) * mm});
            skLineSegment(sketch, "E288", {"start": v(-17.54, -10.3) * mm, "end": v(-18.13, -9.76) * mm});
            skLineSegment(sketch, "E289", {"start": v(-18.13, -9.76) * mm, "end": v(-21.29, -5.26) * mm});
            skLineSegment(sketch, "E290", {"start": v(-21.29, -5.26) * mm, "end": v(-22.18, -3.06) * mm});
            skLineSegment(sketch, "E291", {"start": v(-22.18, -3.06) * mm, "end": v(-23.36, -0.16) * mm});
            skLineSegment(sketch, "E292", {"start": v(-23.36, -0.16) * mm, "end": v(-24.23, 5.27) * mm});
            skLineSegment(sketch, "E293", {"start": v(38.82, 36.37) * mm, "end": v(38.52, 37.92) * mm});
            skLineSegment(sketch, "E294", {"start": v(38.52, 37.92) * mm, "end": v(38.34, 38.82) * mm});
            skLineSegment(sketch, "E295", {"start": v(38.34, 38.82) * mm, "end": v(37.19, 40.6) * mm});
            skLineSegment(sketch, "E296", {"start": v(37.19, 40.6) * mm, "end": v(36.98, 40.9) * mm});
            skLineSegment(sketch, "E297", {"start": v(36.98, 40.9) * mm, "end": v(34.94, 42.33) * mm});
            skLineSegment(sketch, "E298", {"start": v(34.94, 42.33) * mm, "end": v(32.5, 42.88) * mm});
            skLineSegment(sketch, "E299", {"start": v(32.5, 42.88) * mm, "end": v(30.05, 42.48) * mm});
            skLineSegment(sketch, "E300", {"start": v(30.05, 42.48) * mm, "end": v(27.92, 41.18) * mm});
            skLineSegment(sketch, "E301", {"start": v(16.33, -26.34) * mm, "end": v(16.74, -23.35) * mm});
            skLineSegment(sketch, "E302", {"start": v(16.74, -23.35) * mm, "end": v(18.02, -20.63) * mm});
            skLineSegment(sketch, "E303", {"start": v(18.02, -20.63) * mm, "end": v(20.06, -18.4) * mm});
            skLineSegment(sketch, "E304", {"start": v(-38.18, 28.5) * mm, "end": v(-40.33, 27.4) * mm});
            skLineSegment(sketch, "E305", {"start": v(-40.33, 27.4) * mm, "end": v(-44.91, 25.08) * mm});
            skLineSegment(sketch, "E306", {"start": v(14.49, 32.44) * mm, "end": v(13.9, 32.44) * mm});
            skLineSegment(sketch, "E307", {"start": v(13.9, 32.44) * mm, "end": v(7.18, 32.45) * mm});
            skLineSegment(sketch, "E308", {"start": v(7.18, 32.45) * mm, "end": v(-1.34, 32.46) * mm});
            skLineSegment(sketch, "E309", {"start": v(-1.34, 32.46) * mm, "end": v(-14.09, 32.48) * mm});
            skLineSegment(sketch, "E310", {"start": v(21.26, 35.07) * mm, "end": v(18.12, 33.11) * mm});
            skLineSegment(sketch, "E311", {"start": v(18.12, 33.11) * mm, "end": v(14.49, 32.44) * mm});
            skLineSegment(sketch, "E312", {"start": v(-27.19, 41.2) * mm, "end": v(-27.63, 41.47) * mm});
            skLineSegment(sketch, "E313", {"start": v(-27.63, 41.47) * mm, "end": v(-29.3, 42.55) * mm});
            skLineSegment(sketch, "E314", {"start": v(-29.3, 42.55) * mm, "end": v(-29.3, 42.55) * mm});
            skLineSegment(sketch, "E315", {"start": v(-29.3, 42.55) * mm, "end": v(-31.78, 43) * mm});
            skLineSegment(sketch, "E316", {"start": v(-31.78, 43) * mm, "end": v(-34.24, 42.48) * mm});
            skLineSegment(sketch, "E317", {"start": v(-34.24, 42.48) * mm, "end": v(-36.31, 41.06) * mm});
            skLineSegment(sketch, "E318", {"start": v(-36.31, 41.06) * mm, "end": v(-36.83, 40.28) * mm});
            skLineSegment(sketch, "E319", {"start": v(-36.83, 40.28) * mm, "end": v(-37.7, 38.96) * mm});
            skLineSegment(sketch, "E320", {"start": v(-37.7, 38.96) * mm, "end": v(-37.9, 37.92) * mm});
            skLineSegment(sketch, "E321", {"start": v(-37.9, 37.92) * mm, "end": v(-38.18, 36.5) * mm});
            skLineSegment(sketch, "E322", {"start": v(-3.58, -36.78) * mm, "end": v(-3.51, -36.07) * mm});
            skLineSegment(sketch, "E323", {"start": v(3.43, -36.12) * mm, "end": v(3.5, -37.01) * mm});
            skLineSegment(sketch, "E324", {"start": v(-32, 37.94) * mm, "end": v(-31.37, 37.94) * mm});
            skLineSegment(sketch, "E325", {"start": v(-31.37, 37.94) * mm, "end": v(-31.34, 37.92) * mm});
            skLineSegment(sketch, "E326", {"start": v(-31.34, 37.92) * mm, "end": v(-30.8, 37.68) * mm});
            skLineSegment(sketch, "E327", {"start": v(-30.8, 37.68) * mm, "end": v(-30.38, 37.22) * mm});
            skLineSegment(sketch, "E328", {"start": v(-30.38, 37.22) * mm, "end": v(-30.2, 36.62) * mm});
            skLineSegment(sketch, "E329", {"start": v(-30.2, 36.62) * mm, "end": v(-30.26, 36) * mm});
            skLineSegment(sketch, "E330", {"start": v(-30.26, 36) * mm, "end": v(-30.57, 35.46) * mm});
            skLineSegment(sketch, "E331", {"start": v(-30.57, 35.46) * mm, "end": v(-31.07, 35.1) * mm});
            skLineSegment(sketch, "E332", {"start": v(-31.07, 35.1) * mm, "end": v(-31.68, 34.97) * mm});
            skLineSegment(sketch, "E333", {"start": v(-31.68, 34.97) * mm, "end": v(-32.3, 35.1) * mm});
            skLineSegment(sketch, "E334", {"start": v(-32.3, 35.1) * mm, "end": v(-32.8, 35.46) * mm});
            skLineSegment(sketch, "E335", {"start": v(-32.8, 35.46) * mm, "end": v(-33.11, 36) * mm});
            skLineSegment(sketch, "E336", {"start": v(-33.11, 36) * mm, "end": v(-33.18, 36.62) * mm});
            skLineSegment(sketch, "E337", {"start": v(-33.18, 36.62) * mm, "end": v(-32.98, 37.22) * mm});
            skLineSegment(sketch, "E338", {"start": v(-32.98, 37.22) * mm, "end": v(-32.57, 37.68) * mm});
            skLineSegment(sketch, "E339", {"start": v(-32.57, 37.68) * mm, "end": v(-32.03, 37.92) * mm});
            skLineSegment(sketch, "E340", {"start": v(-32.03, 37.92) * mm, "end": v(-32, 37.94) * mm});
            skLineSegment(sketch, "E341", {"start": v(-41.97, 17.78) * mm, "end": v(-42.58, 17.91) * mm});
            skLineSegment(sketch, "E342", {"start": v(-42.58, 17.91) * mm, "end": v(-43.08, 18.28) * mm});
            skLineSegment(sketch, "E343", {"start": v(-43.08, 18.28) * mm, "end": v(-43.4, 18.82) * mm});
            skLineSegment(sketch, "E344", {"start": v(-43.4, 18.82) * mm, "end": v(-43.46, 19.44) * mm});
            skLineSegment(sketch, "E345", {"start": v(-43.46, 19.44) * mm, "end": v(-43.27, 20.03) * mm});
            skLineSegment(sketch, "E346", {"start": v(-43.27, 20.03) * mm, "end": v(-42.85, 20.5) * mm});
            skLineSegment(sketch, "E347", {"start": v(-42.85, 20.5) * mm, "end": v(-42.67, 20.58) * mm});
            skLineSegment(sketch, "E348", {"start": v(-42.67, 20.58) * mm, "end": v(-42.28, 20.75) * mm});
            skLineSegment(sketch, "E349", {"start": v(-42.28, 20.75) * mm, "end": v(-41.66, 20.75) * mm});
            skLineSegment(sketch, "E350", {"start": v(-41.66, 20.75) * mm, "end": v(-41.27, 20.58) * mm});
            skLineSegment(sketch, "E351", {"start": v(-41.27, 20.58) * mm, "end": v(-41.09, 20.5) * mm});
            skLineSegment(sketch, "E352", {"start": v(-41.09, 20.5) * mm, "end": v(-40.67, 20.03) * mm});
            skLineSegment(sketch, "E353", {"start": v(-40.67, 20.03) * mm, "end": v(-40.48, 19.44) * mm});
            skLineSegment(sketch, "E354", {"start": v(-40.48, 19.44) * mm, "end": v(-40.54, 18.82) * mm});
            skLineSegment(sketch, "E355", {"start": v(-40.54, 18.82) * mm, "end": v(-40.85, 18.28) * mm});
            skLineSegment(sketch, "E356", {"start": v(-40.85, 18.28) * mm, "end": v(-41.36, 17.91) * mm});
            skLineSegment(sketch, "E357", {"start": v(-41.36, 17.91) * mm, "end": v(-41.97, 17.78) * mm});
            skSolve(sketch);
        }
        {
            var Q0;
            Q0=makeQuery(id+"F0.imprint","IMPRINT",FACE,{"disambiguationData":[TD([[makeQuery(id+"F0.imprint","IMPRINT",EDGE,{"derivedFrom":sQuery(id+"F0.wireOp",EDGE,"E0")}),1.0]])]});
            extrude(context, id + "F1", {"entities" : qUnion([Q0]), "depth" : 3 * mm, "offsetDistance" : 25 * mm});
        }
    });
